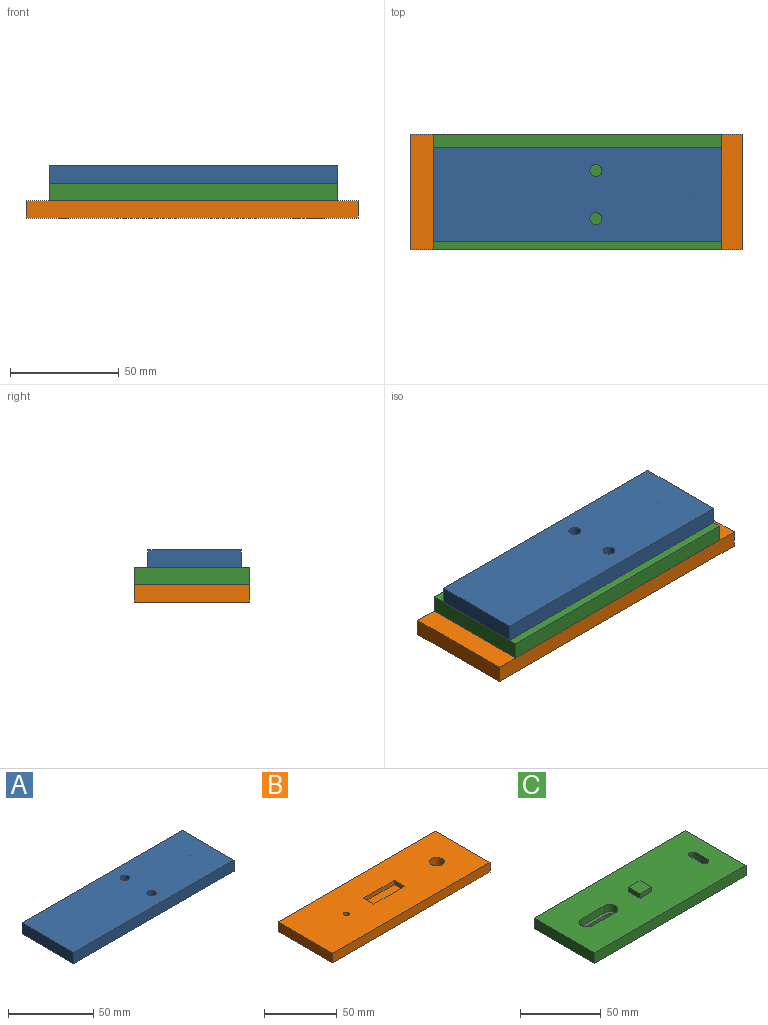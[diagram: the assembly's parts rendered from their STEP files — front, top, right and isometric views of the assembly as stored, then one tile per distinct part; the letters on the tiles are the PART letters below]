
ASSEMBLY  parts=3 mates=2
PART A: 15 faces, bbox 133x43x8 mm
  f0: plane 133x8mm, normal (0,1,0), area 1064mm2, adj f1,f7,f8,f9
  f1: plane 43x8mm, normal (-1,0,0), area 344mm2, adj f0,f2,f8,f9
  f2: plane 133x8mm, normal (0,-1,0), area 1064mm2, adj f1,f7,f8,f9
  f3: plane 20x3.5mm, normal (-1,0,0), area 70mm2, adj f4,f6,f8,f10
  f4: plane 10x3.5mm, normal (0,1,0), area 35mm2, adj f3,f5,f8,f10
  f5: plane 20x3.5mm, normal (1,0,0), area 70mm2, adj f4,f6,f8,f10
  f6: plane 10x3.5mm, normal (0,-1,0), area 35mm2, adj f3,f5,f8,f10
  f7: plane 43x8mm, normal (1,0,0), area 344mm2, adj f0,f2,f8,f9
  f8: plane 133x43mm, normal (0,0,-1), area 5457.6mm2, adj f0,f1,f2,f3,f4,f5,f6,f7
  f9: plane 133x43mm, normal (0,0,1), area 5671.5mm2, adj f0,f1,f2,f7,f11,f12
  f10: plane 20x10mm, normal (0,0,-1), area 200mm2, adj f3,f4,f5,f6
  f11: cylinder r=2.75mm len=8mm, axis (0,0,1), area 138.2mm2, adj f8,f9
  f12: cylinder r=2.75mm len=8mm, axis (0,0,1), area 138.2mm2, adj f8,f9
  f13: cone r=0mm half-angle=59deg, axis (0,0,-1), area 16.2mm2, adj f14
  f14: cylinder r=2.1mm len=6.7mm, axis (0,0,-1), area 88.4mm2, adj f8,f13
PART B: 22 faces, bbox 153x53x8 mm
  f0: plane 153x53mm, normal (0,0,1), area 7716.6mm2, adj f10,f11,f12,f13,f14,f15,f16,f17
  f1: plane 153x53mm, normal (0,0,-1), area 7975mm2, adj f3,f5,f7,f9,f10,f11,f12,f13
  f2: cone r=0mm half-angle=59deg, axis (0,0,-1), area 16.2mm2, adj f3
  f3: cylinder r=2.1mm len=5.3mm, axis (0,0,-1), area 69.9mm2, adj f1,f2
  f4: cone r=0mm half-angle=59deg, axis (0,0,-1), area 16.2mm2, adj f5
  f5: cylinder r=2.1mm len=5.3mm, axis (0,0,-1), area 69.9mm2, adj f1,f4
  f6: cone r=0mm half-angle=59deg, axis (0,0,-1), area 16.2mm2, adj f7
  f7: cylinder r=2.1mm len=5.3mm, axis (0,0,-1), area 69.9mm2, adj f1,f6
  f8: cone r=0mm half-angle=59deg, axis (0,0,-1), area 16.2mm2, adj f9
  f9: cylinder r=2.1mm len=5.3mm, axis (0,0,-1), area 69.9mm2, adj f1,f8
  f10: plane 53x8mm, normal (1,0,0), area 424mm2, adj f0,f1,f12,f13
  f11: plane 53x8mm, normal (-1,0,0), area 424mm2, adj f0,f1,f12,f13
  f12: plane 153x8mm, normal (0,-1,0), area 1224mm2, adj f0,f1,f10,f11
  f13: plane 153x8mm, normal (0,1,0), area 1224mm2, adj f0,f1,f10,f11
  f14: plane 30x3.5mm, normal (0,-1,0), area 105mm2, adj f0,f15,f17,f18
  f15: plane 10x3.5mm, normal (1,0,0), area 35mm2, adj f0,f14,f16,f18
  f16: plane 30x3.5mm, normal (0,1,0), area 105mm2, adj f0,f15,f17,f18
  f17: plane 10x3.5mm, normal (-1,0,0), area 35mm2, adj f0,f14,f16,f18
  f18: plane 30x10mm, normal (0,0,1), area 300mm2, adj f14,f15,f16,f17
  f19: cone r=0mm half-angle=59deg, axis (0,0,1), area 16.2mm2, adj f20
  f20: cylinder r=2.1mm len=6.7mm, axis (0,0,1), area 88.4mm2, adj f0,f19
  f21: cylinder r=5mm len=10mm, axis (0,0,1), area 251.3mm2, adj f0,f1
PART C: 34 faces, bbox 133x53x15 mm
  f0: plane 133x53mm, normal (0,0,-1), area 6636.7mm2, adj f2,f3,f4,f5,f7,f8,f9,f10
  f1: plane 133x53mm, normal (0,0,1), area 6591.7mm2, adj f9,f10,f13,f14,f15,f16,f18,f19
  f2: cylinder r=2.75mm len=5.5mm, axis (0,0,1), area 21.6mm2, adj f0,f3,f5,f24
  f3: plane 20x2.5mm, normal (0,1,0), area 50mm2, adj f0,f2,f4,f24
  f4: cylinder r=2.75mm len=5.5mm, axis (0,0,1), area 21.6mm2, adj f0,f3,f5,f24
  f5: plane 20x2.5mm, normal (0,-1,0), area 50mm2, adj f0,f2,f4,f24
  f6: plane 10x10mm, normal (0,0,-1), area 100mm2, adj f7,f8,f11,f12
  f7: plane 10x3.5mm, normal (0,1,0), area 35mm2, adj f0,f6,f11,f12
  f8: plane 10x3.5mm, normal (0,-1,0), area 35mm2, adj f0,f6,f11,f12
  f9: plane 53x8mm, normal (-1,0,0), area 424mm2, adj f0,f1,f18,f19
  f10: plane 53x8mm, normal (1,0,0), area 424mm2, adj f0,f1,f18,f19
  f11: plane 10x3.5mm, normal (1,0,0), area 35mm2, adj f0,f6,f7,f8
  f12: plane 10x3.5mm, normal (-1,0,0), area 35mm2, adj f0,f6,f7,f8
  f13: plane 10x3.5mm, normal (0,-1,0), area 35mm2, adj f1,f14,f16,f17
  f14: plane 10x3.5mm, normal (1,0,0), area 35mm2, adj f1,f13,f15,f17
  f15: plane 10x3.5mm, normal (0,1,0), area 35mm2, adj f1,f14,f16,f17
  f16: plane 10x3.5mm, normal (-1,0,0), area 35mm2, adj f1,f13,f15,f17
  f17: plane 10x10mm, normal (0,0,1), area 100mm2, adj f13,f14,f15,f16
  f18: plane 133x8mm, normal (0,-1,0), area 1064mm2, adj f0,f1,f9,f10
  f19: plane 133x8mm, normal (0,1,0), area 1064mm2, adj f0,f1,f9,f10
  f20: plane 20x5.5mm, normal (0,-1,0), area 110mm2, adj f1,f21,f23,f24
  f21: cylinder r=5mm len=10mm, axis (0,0,1), area 86.4mm2, adj f1,f20,f22,f24
  f22: plane 20x5.5mm, normal (0,1,0), area 110mm2, adj f1,f21,f23,f24
  f23: cylinder r=5mm len=10mm, axis (0,0,1), area 86.4mm2, adj f1,f20,f22,f24
  f24: plane 30x10mm, normal (0,0,1), area 144.8mm2, adj f2,f3,f4,f5,f20,f21,f22,f23
  f25: plane 10x2.5mm, normal (1,0,0), area 25mm2, adj f1,f26,f28,f33
  f26: cylinder r=2.75mm len=5.5mm, axis (0,0,-1), area 21.6mm2, adj f1,f25,f27,f33
  f27: plane 10x2.5mm, normal (-1,0,0), area 25mm2, adj f1,f26,f28,f33
  f28: cylinder r=2.75mm len=5.5mm, axis (0,0,-1), area 21.6mm2, adj f1,f25,f27,f33
  f29: plane 10x5.5mm, normal (1,0,0), area 55mm2, adj f0,f30,f32,f33
  f30: cylinder r=5mm len=10mm, axis (0,0,-1), area 86.4mm2, adj f0,f29,f31,f33
  f31: plane 10x5.5mm, normal (-1,0,0), area 55mm2, adj f0,f30,f32,f33
  f32: cylinder r=5mm len=10mm, axis (0,0,-1), area 86.4mm2, adj f0,f29,f31,f33
  f33: plane 20x10mm, normal (0,0,-1), area 99.8mm2, adj f25,f26,f27,f28,f29,f30,f31,f32
PLACE A t=(-75.22,25.15,0.05)mm
PLACE B t=(-75.83,26.37,0.05)mm fixed
PLACE C t=(-75.22,26.37,0.05)mm
MATE pin_slot C.f16 <-> A.f5  axis (-1,0,0) through (-80.22,26.37,17.8)mm
MATE pin_slot C.f8 <-> B.f16  axis (0,-1,0) through (-75.22,21.37,6.3)mm
